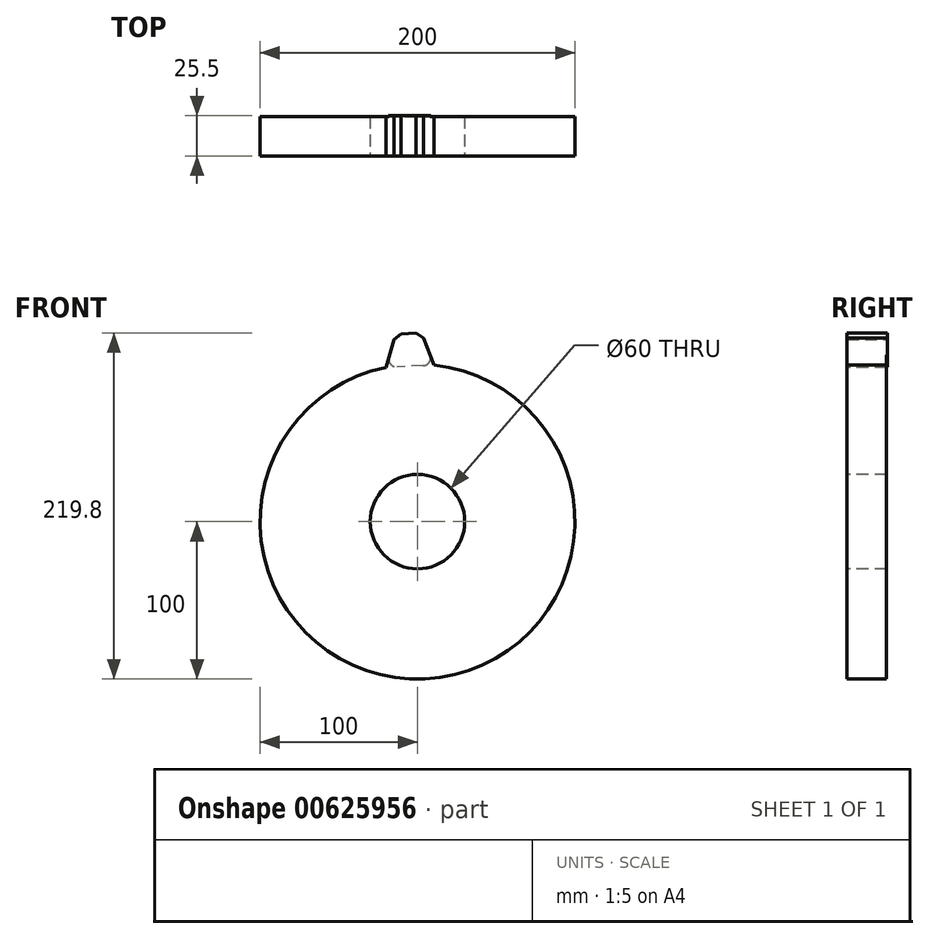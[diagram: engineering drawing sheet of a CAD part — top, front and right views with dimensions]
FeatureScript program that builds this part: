
annotation { "Feature Type Name" : "Feature", "Feature Type Description" : "" }
export const myFeature = defineFeature(function(context is Context, id is Id, definition is map)
    precondition{}
    {
        {
            var Q0;
            Q0=qCreatedBy(makeId("Front.planeOp"),FACE);
            var sketch = newSketch(context, id + "F0", { "sketchPlane" : qUnion([Q0])});
            skCircle(sketch, "E0", {"center": v(0, 0) * mm, "radius": 100 * mm});
            skSolve(sketch);
        }
        {
            var Q0;
            Q0=makeQuery(id+"F0.imprint","IMPRINT",FACE,{"disambiguationData":[TD([[makeQuery(id+"F0.imprint","IMPRINT",EDGE,{"derivedFrom":sQuery(id+"F0.wireOp",EDGE,"E0")}),1.0]])]});
            extrude(context, id + "F1", {"entities" : qUnion([Q0]), "depth" : 25 * mm, "offsetDistance" : 25 * mm});
        }
        {
            var Q0;
            Q0=makeQuery(id+"F1.opExtrude","CAP_FACE",FACE,{"disambiguationData":[OSD([sQuery(id+"F0.wireOp",EDGE,"E0")])],"isStart":false});
            var sketch = newSketch(context, id + "F2", { "sketchPlane" : qUnion([Q0])});
            skCircle(sketch, "E1", {"center": v(0, 0) * mm, "radius": 120 * mm, "construction": true});
            skLineSegment(sketch, "E2", {"start": v(-19.95, 97.99) * mm, "end": v(-14.1, 119.17) * mm});
            skLineSegment(sketch, "E3", {"start": v(-14.1, 119.17) * mm, "end": v(2.68, 119.97) * mm});
            skLineSegment(sketch, "E4", {"start": v(2.68, 119.97) * mm, "end": v(10.52, 99.44) * mm});
            skLineSegment(sketch, "E5", {"start": v(10.52, 99.44) * mm, "end": v(-19.95, 97.99) * mm});
            skSolve(sketch);
        }
        {
            var Q0;
            Q0 = qSketchRegion(id + "F2", true);
            extrude(context, id + "F3", {"entities" : qUnion([Q0]), "operationType" : NewBodyOperationType.ADD, "oppositeDirection" : true, "depth" : 25.5 * mm, "offsetDistance" : 25 * mm});
        }
        {
            var Q0;
            Q0=makeQuery(id+"F3.opExtrude","SWEPT_EDGE",EDGE,{"disambiguationData":[OSD([sQuery(id+"F2.wireOp",EDGE,"E3"),sQuery(id+"F2.wireOp",EDGE,"E4")])]});
            var Q1;
            Q1=makeQuery(id+"F3.opExtrude","SWEPT_EDGE",EDGE,{"disambiguationData":[OSD([sQuery(id+"F2.wireOp",EDGE,"E2"),sQuery(id+"F2.wireOp",EDGE,"E3")])]});
            chamfer(context, id + "F4", {"entities" : qUnion([Q0, Q1]), "width" : 5 * mm, "tangentPropagation" : true});
        }
        {
            var Q0;
            {var subQ0=sQuery(id+"F0.wireOp",EDGE,"E0");var subQ1=sQuery(id+"F2.wireOp",EDGE,"E2");Q0=makeQuery(id+"F3.boolean.opBoolean","SPLIT",EDGE,{"disambiguationData":[topologyDisambiguationEdgeConnected([makeQuery(id+"F1.opExtrude","SWEPT_FACE",FACE,{"disambiguationData":[OSD([subQ0])]})])],"derivedFrom":makeQuery(id+"F3.opExtrude","SWEPT_EDGE",EDGE,{"disambiguationData":[OSD([subQ0,subQ1,sQuery(id+"F2.wireOp",EDGE,"E5")])]})});}
            var Q1;
            {var subQ0=sQuery(id+"F0.wireOp",EDGE,"E0");var subQ1=sQuery(id+"F2.wireOp",EDGE,"E4");Q1=makeQuery(id+"F3.boolean.opBoolean","SPLIT",EDGE,{"disambiguationData":[topologyDisambiguationEdgeConnected([makeQuery(id+"F1.opExtrude","SWEPT_FACE",FACE,{"disambiguationData":[OSD([subQ0])]})])],"derivedFrom":makeQuery(id+"F3.opExtrude","SWEPT_EDGE",EDGE,{"disambiguationData":[OSD([subQ0,subQ1,sQuery(id+"F2.wireOp",EDGE,"E5")])]})});}
            fillet(context, id + "F5", {"entities" : qUnion([Q0, Q1]), "radius" : 5 * mm, "tangentPropagation" : true, "allowEdgeOverflow" : false});
        }
        {
            var Q0;
            Q0=makeQuery(id+"F3.boolean.opBoolean","MERGE",FACE,{"derivedFrom":[makeQuery(id+"F1.opExtrude","CAP_FACE",FACE,{"disambiguationData":[OSD([sQuery(id+"F0.wireOp",EDGE,"E0")])],"isStart":false}),makeQuery(id+"F3.opExtrude","CAP_FACE",FACE,{"disambiguationData":[OSD([sQuery(id+"F2.wireOp",EDGE,"E2"),sQuery(id+"F2.wireOp",EDGE,"E3"),sQuery(id+"F2.wireOp",EDGE,"E4"),sQuery(id+"F2.wireOp",EDGE,"E5")])],"isStart":true})]});
            var sketch = newSketch(context, id + "F6", { "sketchPlane" : qUnion([Q0])});
            skCircle(sketch, "E6", {"center": v(0, 0) * mm, "radius": 30 * mm});
            skSolve(sketch);
        }
        {
            var Q0;
            Q0=makeQuery(id+"F6.imprint","IMPRINT",FACE,{"disambiguationData":[TD([[makeQuery(id+"F6.imprint","IMPRINT",EDGE,{"derivedFrom":sQuery(id+"F6.wireOp",EDGE,"E6")}),1.0]])]});
            var Q1;
            Q1=makeQuery(id+"F1.opExtrude","CAP_FACE",FACE,{"disambiguationData":[OSD([sQuery(id+"F0.wireOp",EDGE,"E0")])],"isStart":true});
            extrude(context, id + "F7", {"entities" : qUnion([Q0, Q1]), "operationType" : NewBodyOperationType.REMOVE, "endBound" : BoundingType.THROUGH_ALL, "oppositeDirection" : true, "depth" : 30 * mm, "offsetDistance" : 25 * mm});
        }
    });
